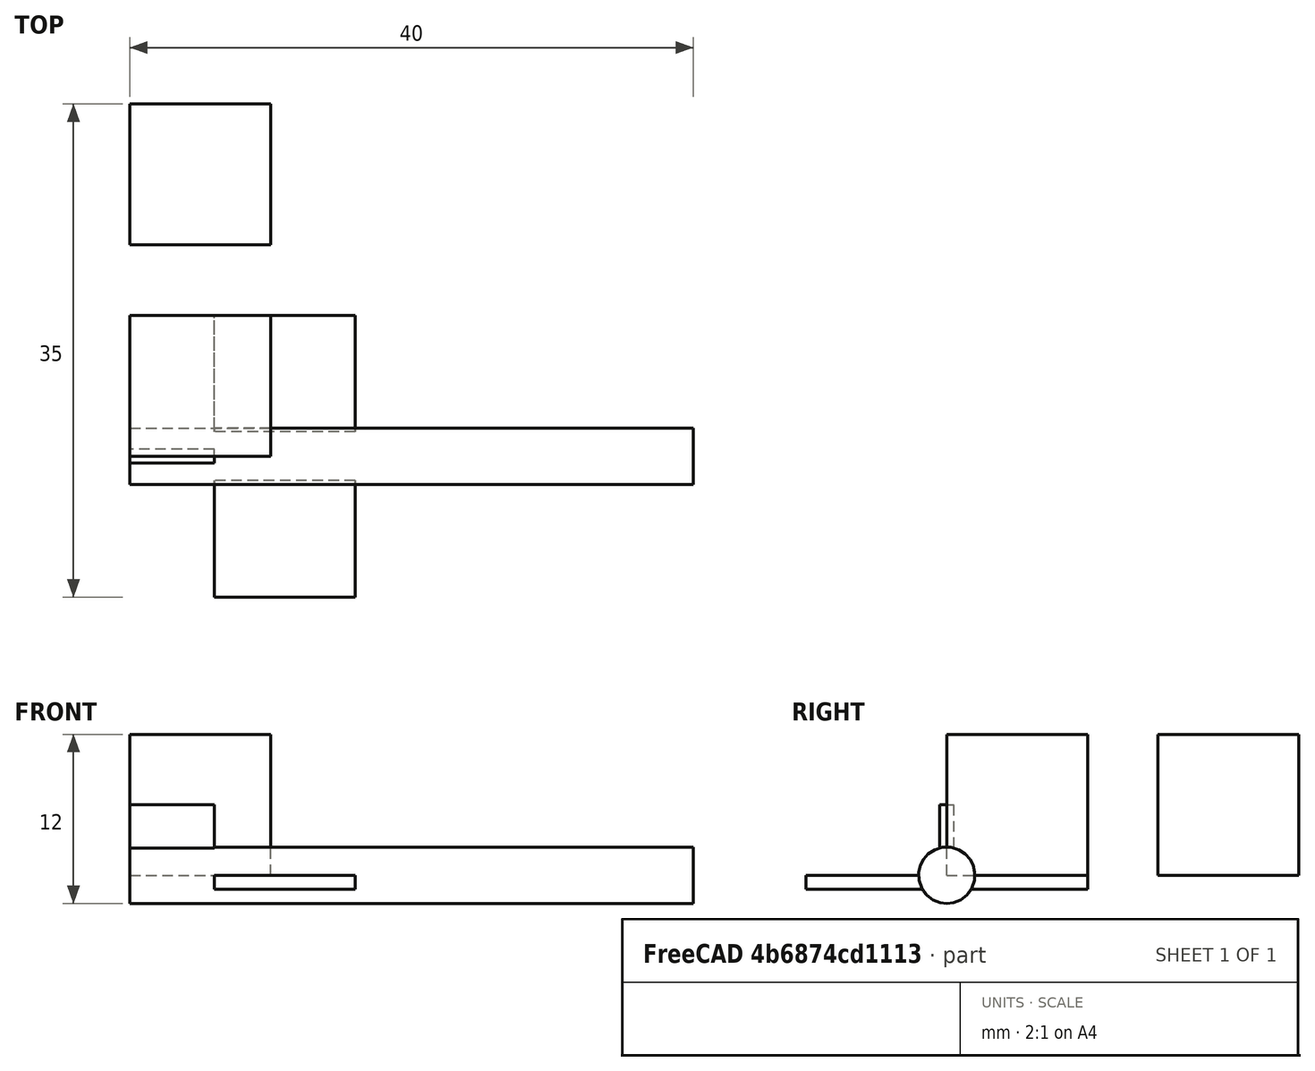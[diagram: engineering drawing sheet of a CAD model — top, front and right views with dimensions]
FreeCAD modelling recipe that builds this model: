
FCSTD DOCUMENT  (FreeCAD 0.21R33694 (Git))
Label: aeroplane_model
License: All rights reserved
LicenseURL: http://en.wikipedia.org/wiki/All_rights_reserved
objects: Part::Box×4, Part::FeaturePython×3, Sketcher::SketchObject×2, Part::Cylinder×1, Part::Fuse×1, Part::MultiFuse×1, Part::Part2DObjectPython×1, Mesh::Feature×1
note: 13 computed .brp shape members not serialized (recipe doc carries the construction recipe); baked Part::Feature solids carry a one-line shape summary decoded from their .brp

FEATURE [Part::Cylinder] Cylinder
  Angle = 360
  AttacherType = Attacher::AttachEngine3D
  FirstAngle = 0
  Height = 20
  Placement = pos=(0,0,0) rot=(0,1,0;1.5708rad)
  Radius = 2
  SecondAngle = 0
FEATURE [Part::Box] Box  label="Cube"
  AttacherType = Attacher::AttachEngine3D
  Height = 1
  Length = 5
  Placement = pos=(3,-10,-1) rot=(0,0,1;0rad)
  Width = 20
FEATURE [Part::Fuse] Fusion
  Base = -> Box
  Tool = -> Cylinder
FEATURE [Part::Box] Box001  label="Cube001"
  AttacherType = Attacher::AttachEngine3D
  Height = 5
  Length = 3
  Placement = pos=(0,-0.5,0) rot=(0,0,1;0rad)
  Width = 1
FEATURE [Part::MultiFuse] Fusion001  label="Aeroplane"
  Shapes = -> [Fusion,Box001]
FEATURE [Part::FeaturePython] Clone  label="Aeroplane001"  # Draft clone (typed FeaturePython)
  AttacherType = Attacher::AttachEngine3D
  Fuse = false
  Objects = -> [Fusion001]
  Scale = (2,1,1)
FEATURE [Part::FeaturePython] PointLight  # WARN: FeaturePython — macro-defined, semantics opaque (R4)
  FadeDistance = 0
  FadePower = 0
  Placement = pos=(10,10,10) rot=(0,0,1;0rad)
FEATURE [Part::Part2DObjectPython] ShapeString  # Draft 2D object (typed FeaturePython)
  FontFile = /Library/Fonts/Arial Unicode.ttf
  MakeFace = true
  Placement = pos=(40.38,1.427e-05,5.29) rot=(0,0.707108,0.707106;3.14159rad)
  Size = 3
  String = Airplane
  Tracking = 0
FEATURE [Sketcher::SketchObject] Sketch
  FullyConstrained = false
  Placement = pos=(1.97e-13,-2.6053e-06,6.808e-12) rot=(1,0,0;0.017453rad)
  sketch-geometry (130):
    g0: LineSegment StartX=38.1366 StartY=-5.29 StartZ=0 EndX=38.4957 EndY=-5.29 EndZ=0
    g1: LineSegment StartX=39.1172 StartY=-7.69699 StartZ=0 EndX=38.1366 EndY=-5.29 EndZ=0
    g2: LineSegment StartX=39.46 StartY=-7.69699 StartZ=0 EndX=39.1172 EndY=-7.69699 EndZ=0
    g3: LineSegment StartX=40.3833 StartY=-5.29 StartZ=0 EndX=39.46 EndY=-7.69699 EndZ=0
    g4: LineSegment StartX=40.0471 StartY=-5.29 StartZ=0 EndX=40.3833 EndY=-5.29 EndZ=0
    g5: LineSegment StartX=39.7814 StartY=-6.02469 StartZ=0 EndX=40.0471 EndY=-5.29 EndZ=0
    g6: LineSegment StartX=38.7778 StartY=-6.02469 StartZ=0 EndX=39.7814 EndY=-6.02469 EndZ=0
    g7: LineSegment StartX=38.4957 StartY=-5.29 StartZ=0 EndX=38.7778 EndY=-6.02469 EndZ=0
    g8: BSplineCurve PolesCount=3 KnotsCount=2 Degree=2 IsPeriodic=0
    g9: LineSegment StartX=39.6912 StartY=-6.27659 StartZ=0 EndX=38.8745 EndY=-6.27659 EndZ=0
    g10: LineSegment StartX=39.4223 StartY=-6.99422 StartZ=0 EndX=39.6912 EndY=-6.27659 EndZ=0
    g11: BSplineCurve PolesCount=3 KnotsCount=2 Degree=2 IsPeriodic=0
    g12: LineSegment StartX=39.2911 StartY=-7.44357 StartZ=0 EndX=39.2993 EndY=-7.44357 EndZ=0
    g13: BSplineCurve PolesCount=3 KnotsCount=2 Degree=2 IsPeriodic=0
    g14: LineSegment StartX=37.6211 StartY=-5.29 StartZ=0 EndX=37.9163 EndY=-5.29 EndZ=0
    g15: LineSegment StartX=37.6211 StartY=-7.03227 StartZ=0 EndX=37.6211 EndY=-5.29 EndZ=0
    g16: LineSegment StartX=37.9163 StartY=-7.03227 StartZ=0 EndX=37.6211 EndY=-7.03227 EndZ=0
    g17: LineSegment StartX=37.9163 StartY=-5.29 StartZ=0 EndX=37.9163 EndY=-7.03227 EndZ=0
    g18: LineSegment StartX=37.6211 StartY=-7.36113 StartZ=0 EndX=37.9163 EndY=-7.36113 EndZ=0
    g19: LineSegment StartX=37.6211 StartY=-7.69699 StartZ=0 EndX=37.6211 EndY=-7.36113 EndZ=0
    g20: LineSegment StartX=37.9163 StartY=-7.69699 StartZ=0 EndX=37.6211 EndY=-7.69699 EndZ=0
    g21: LineSegment StartX=37.9163 StartY=-7.36113 StartZ=0 EndX=37.9163 EndY=-7.69699 EndZ=0
    g22: LineSegment StartX=36.2295 StartY=-6.98121 StartZ=0 EndX=36.3312 EndY=-6.71041 EndZ=0
    g23: BSplineCurve PolesCount=3 KnotsCount=2 Degree=2 IsPeriodic=0
    g24: BSplineCurve PolesCount=3 KnotsCount=2 Degree=2 IsPeriodic=0
    g25: LineSegment StartX=36.9085 StartY=-6.77163 StartZ=0 EndX=36.9019 EndY=-6.77163 EndZ=0
    g26: LineSegment StartX=36.9085 StartY=-7.03227 StartZ=0 EndX=36.9085 EndY=-6.77163 EndZ=0
    g27: LineSegment StartX=37.1774 StartY=-7.03227 StartZ=0 EndX=36.9085 EndY=-7.03227 EndZ=0
    g28: LineSegment StartX=37.1774 StartY=-5.29 StartZ=0 EndX=37.1774 EndY=-7.03227 EndZ=0
    g29: LineSegment StartX=36.8822 StartY=-5.29 StartZ=0 EndX=37.1774 EndY=-5.29 EndZ=0
    g30: LineSegment StartX=36.8822 StartY=-6.20705 StartZ=0 EndX=36.8822 EndY=-5.29 EndZ=0
    g31: BSplineCurve PolesCount=3 KnotsCount=2 Degree=2 IsPeriodic=0
    g32: BSplineCurve PolesCount=3 KnotsCount=2 Degree=2 IsPeriodic=0
    g33: BSplineCurve PolesCount=3 KnotsCount=2 Degree=2 IsPeriodic=0
    g34: BSplineCurve PolesCount=3 KnotsCount=2 Degree=2 IsPeriodic=0
    g35: LineSegment StartX=35.7758 StartY=-6.81055 StartZ=0 EndX=35.7692 EndY=-6.81055 EndZ=0
    g36: LineSegment StartX=35.7758 StartY=-7.03227 StartZ=0 EndX=35.7758 EndY=-6.81055 EndZ=0
    g37: LineSegment StartX=36.0448 StartY=-7.03227 StartZ=0 EndX=35.7758 EndY=-7.03227 EndZ=0
    g38: LineSegment StartX=36.0448 StartY=-4.61828 StartZ=0 EndX=36.0448 EndY=-7.03227 EndZ=0
    g39: LineSegment StartX=35.7496 StartY=-4.61828 StartZ=0 EndX=36.0448 EndY=-4.61828 EndZ=0
    g40: LineSegment StartX=35.7496 StartY=-5.46667 StartZ=0 EndX=35.7496 EndY=-4.61828 EndZ=0
    g41: LineSegment StartX=35.7414 StartY=-5.46667 StartZ=0 EndX=35.7496 EndY=-5.46667 EndZ=0
    g42: BSplineCurve PolesCount=3 KnotsCount=2 Degree=2 IsPeriodic=0
    g43: BSplineCurve PolesCount=3 KnotsCount=2 Degree=2 IsPeriodic=0
    g44: BSplineCurve PolesCount=3 KnotsCount=2 Degree=2 IsPeriodic=0
    g45: BSplineCurve PolesCount=3 KnotsCount=2 Degree=2 IsPeriodic=0
    g46: BSplineCurve PolesCount=3 KnotsCount=2 Degree=2 IsPeriodic=0
    g47: BSplineCurve PolesCount=3 KnotsCount=2 Degree=2 IsPeriodic=0
    g48: BSplineCurve PolesCount=3 KnotsCount=2 Degree=2 IsPeriodic=0
    g49: BSplineCurve PolesCount=3 KnotsCount=2 Degree=2 IsPeriodic=0
    g50: BSplineCurve PolesCount=3 KnotsCount=2 Degree=2 IsPeriodic=0
    g51: BSplineCurve PolesCount=3 KnotsCount=2 Degree=2 IsPeriodic=0
    g52: BSplineCurve PolesCount=3 KnotsCount=2 Degree=2 IsPeriodic=0
    g53: BSplineCurve PolesCount=3 KnotsCount=2 Degree=2 IsPeriodic=0
    g54: BSplineCurve PolesCount=3 KnotsCount=2 Degree=2 IsPeriodic=0
    g55: LineSegment StartX=33.8846 StartY=-5.29 StartZ=0 EndX=34.1798 EndY=-5.29 EndZ=0
    g56: LineSegment StartX=33.8846 StartY=-7.69699 StartZ=0 EndX=33.8846 EndY=-5.29 EndZ=0
    g57: LineSegment StartX=34.1798 StartY=-7.69699 StartZ=0 EndX=33.8846 EndY=-7.69699 EndZ=0
    g58: LineSegment StartX=34.1798 StartY=-5.29 StartZ=0 EndX=34.1798 EndY=-7.69699 EndZ=0
    g59: LineSegment StartX=31.9224 StartY=-5.29 StartZ=0 EndX=32.2323 EndY=-5.29 EndZ=0
    g60: BSplineCurve PolesCount=3 KnotsCount=2 Degree=2 IsPeriodic=0
    g61: BSplineCurve PolesCount=3 KnotsCount=2 Degree=2 IsPeriodic=0
    g62: LineSegment StartX=32.0175 StartY=-6.41806 StartZ=0 EndX=32.0175 EndY=-6.0201 EndZ=0
    g63: BSplineCurve PolesCount=3 KnotsCount=2 Degree=2 IsPeriodic=0
    g64: BSplineCurve PolesCount=3 KnotsCount=2 Degree=2 IsPeriodic=0
    g65: BSplineCurve PolesCount=3 KnotsCount=2 Degree=2 IsPeriodic=0
    g66: BSplineCurve PolesCount=3 KnotsCount=2 Degree=2 IsPeriodic=0
    g67: BSplineCurve PolesCount=3 KnotsCount=2 Degree=2 IsPeriodic=0
    g68: LineSegment StartX=33.1884 StartY=-6.50049 StartZ=0 EndX=33.477 EndY=-6.53821 EndZ=0
    g69: BSplineCurve PolesCount=3 KnotsCount=2 Degree=2 IsPeriodic=0
    g70: BSplineCurve PolesCount=3 KnotsCount=2 Degree=2 IsPeriodic=0
    g71: BSplineCurve PolesCount=3 KnotsCount=2 Degree=2 IsPeriodic=0
    g72: BSplineCurve PolesCount=3 KnotsCount=2 Degree=2 IsPeriodic=0
    g73: BSplineCurve PolesCount=3 KnotsCount=2 Degree=2 IsPeriodic=0
    g74: BSplineCurve PolesCount=3 KnotsCount=2 Degree=2 IsPeriodic=0
    g75: BSplineCurve PolesCount=3 KnotsCount=2 Degree=2 IsPeriodic=0
    g76: LineSegment StartX=32.8424 StartY=-6.29375 StartZ=0 EndX=32.5669 EndY=-6.33475 EndZ=0
    g77: BSplineCurve PolesCount=3 KnotsCount=2 Degree=2 IsPeriodic=0
    g78: BSplineCurve PolesCount=3 KnotsCount=2 Degree=2 IsPeriodic=0
    g79: BSplineCurve PolesCount=3 KnotsCount=2 Degree=2 IsPeriodic=0
    g80: BSplineCurve PolesCount=3 KnotsCount=2 Degree=2 IsPeriodic=0
    g81: BSplineCurve PolesCount=3 KnotsCount=2 Degree=2 IsPeriodic=0
    g82: BSplineCurve PolesCount=3 KnotsCount=2 Degree=2 IsPeriodic=0
    g83: LineSegment StartX=32.3127 StartY=-6.05246 StartZ=0 EndX=32.3127 EndY=-6.15764 EndZ=0
    g84: BSplineCurve PolesCount=3 KnotsCount=2 Degree=2 IsPeriodic=0
    g85: BSplineCurve PolesCount=3 KnotsCount=2 Degree=2 IsPeriodic=0
    g86: BSplineCurve PolesCount=3 KnotsCount=2 Degree=2 IsPeriodic=0
    g87: BSplineCurve PolesCount=3 KnotsCount=2 Degree=2 IsPeriodic=0
    g88: BSplineCurve PolesCount=3 KnotsCount=2 Degree=2 IsPeriodic=0
    g89: BSplineCurve PolesCount=3 KnotsCount=2 Degree=2 IsPeriodic=0
    g90: LineSegment StartX=30.1411 StartY=-5.29 StartZ=0 EndX=30.4379 EndY=-5.29 EndZ=0
    g91: LineSegment StartX=30.1411 StartY=-6.36383 StartZ=0 EndX=30.1411 EndY=-5.29 EndZ=0
    g92: BSplineCurve PolesCount=3 KnotsCount=2 Degree=2 IsPeriodic=0
    g93: BSplineCurve PolesCount=3 KnotsCount=2 Degree=2 IsPeriodic=0
    g94: BSplineCurve PolesCount=3 KnotsCount=2 Degree=2 IsPeriodic=0
    g95: BSplineCurve PolesCount=3 KnotsCount=2 Degree=2 IsPeriodic=0
    g96: BSplineCurve PolesCount=3 KnotsCount=2 Degree=2 IsPeriodic=0
    g97: BSplineCurve PolesCount=3 KnotsCount=2 Degree=2 IsPeriodic=0
    g98: LineSegment StartX=31.294 StartY=-6.78814 StartZ=0 EndX=31.2874 EndY=-6.78814 EndZ=0
    g99: LineSegment StartX=31.294 StartY=-7.03227 StartZ=0 EndX=31.294 EndY=-6.78814 EndZ=0
    g100: LineSegment StartX=31.5596 StartY=-7.03227 StartZ=0 EndX=31.294 EndY=-7.03227 EndZ=0
    g101: LineSegment StartX=31.5596 StartY=-5.29 StartZ=0 EndX=31.5596 EndY=-7.03227 EndZ=0
    g102: LineSegment StartX=31.2644 StartY=-5.29 StartZ=0 EndX=31.5596 EndY=-5.29 EndZ=0
    g103: LineSegment StartX=31.2644 StartY=-6.24565 StartZ=0 EndX=31.2644 EndY=-5.29 EndZ=0
    g104: BSplineCurve PolesCount=3 KnotsCount=2 Degree=2 IsPeriodic=0
    g105: BSplineCurve PolesCount=3 KnotsCount=2 Degree=2 IsPeriodic=0
    g106: BSplineCurve PolesCount=3 KnotsCount=2 Degree=2 IsPeriodic=0
    g107: BSplineCurve PolesCount=3 KnotsCount=2 Degree=2 IsPeriodic=0
    g108: BSplineCurve PolesCount=3 KnotsCount=2 Degree=2 IsPeriodic=0
    g109: LineSegment StartX=30.4379 StartY=-5.29 StartZ=0 EndX=30.4379 EndY=-6.35279 EndZ=0
    g110: LineSegment StartX=28.1827 StartY=-6.08767 StartZ=0 EndX=29.4864 EndY=-6.08767 EndZ=0
    g111: BSplineCurve PolesCount=3 KnotsCount=2 Degree=2 IsPeriodic=0
    g112: BSplineCurve PolesCount=3 KnotsCount=2 Degree=2 IsPeriodic=0
    g113: BSplineCurve PolesCount=3 KnotsCount=2 Degree=2 IsPeriodic=0
    g114: BSplineCurve PolesCount=3 KnotsCount=2 Degree=2 IsPeriodic=0
    g115: BSplineCurve PolesCount=3 KnotsCount=2 Degree=2 IsPeriodic=0
    g116: BSplineCurve PolesCount=3 KnotsCount=2 Degree=2 IsPeriodic=0
    g117: BSplineCurve PolesCount=3 KnotsCount=2 Degree=2 IsPeriodic=0
    g118: BSplineCurve PolesCount=3 KnotsCount=2 Degree=2 IsPeriodic=0
    g119: BSplineCurve PolesCount=3 KnotsCount=2 Degree=2 IsPeriodic=0
    g120: LineSegment StartX=28.4959 StartY=-5.84976 StartZ=0 EndX=28.1925 EndY=-5.81205 EndZ=0
    g121: BSplineCurve PolesCount=3 KnotsCount=2 Degree=2 IsPeriodic=0
    g122: BSplineCurve PolesCount=3 KnotsCount=2 Degree=2 IsPeriodic=0
    g123: BSplineCurve PolesCount=3 KnotsCount=2 Degree=2 IsPeriodic=0
    g124: BSplineCurve PolesCount=3 KnotsCount=2 Degree=2 IsPeriodic=0
    g125: BSplineCurve PolesCount=3 KnotsCount=2 Degree=2 IsPeriodic=0
    g126: LineSegment StartX=29.47 StartY=-6.32557 StartZ=0 EndX=28.4861 EndY=-6.32557 EndZ=0
    g127: BSplineCurve PolesCount=3 KnotsCount=2 Degree=2 IsPeriodic=0
    g128: BSplineCurve PolesCount=3 KnotsCount=2 Degree=2 IsPeriodic=0
    g129: BSplineCurve PolesCount=3 KnotsCount=2 Degree=2 IsPeriodic=0
  constraints (172):
    c: Horizontal(g0)
    c: Coincident(g0,g1)
    c: Coincident(g1,g2)
    c: Horizontal(g2)
    c: Coincident(g2,g3)
    c: Coincident(g3,g4)
    c: Horizontal(g4)
    c: Coincident(g4,g5)
    c: Coincident(g5,g6)
    c: Horizontal(g6)
    c: Coincident(g6,g7)
    c: Coincident(g7,g0)
    c: Coincident(g8,g9)
    c: Horizontal(g9)
    c: Coincident(g9,g10)
    c: Coincident(g10,g11)
    c: Coincident(g11,g12)
    c: Horizontal(g12)
    c: Coincident(g12,g13)
    c: Coincident(g13,g8)
    c: Horizontal(g14)
    c: Coincident(g14,g15)
    c: Vertical(g15)
    c: Coincident(g15,g16)
    c: Horizontal(g16)
    c: Coincident(g16,g17)
    c: Vertical(g17)
    c: Coincident(g17,g14)
    c: Horizontal(g18)
    c: Coincident(g18,g19)
    c: Vertical(g19)
    c: Coincident(g19,g20)
    c: Horizontal(g20)
    c: Coincident(g20,g21)
    c: Coincident(g21,g18)
    c: Coincident(g22,g23)
    c: Coincident(g23,g24)
    c: Coincident(g24,g25)
    c: Horizontal(g25)
    c: Coincident(g25,g26)
    c: Vertical(g26)
    c: Coincident(g26,g27)
    c: Horizontal(g27)
    c: Coincident(g27,g28)
    c: Vertical(g28)
    c: Coincident(g28,g29)
    c: Horizontal(g29)
    c: Coincident(g29,g30)
    c: Coincident(g30,g31)
    c: Coincident(g31,g32)
    c: Coincident(g32,g33)
    c: Coincident(g33,g22)
    c: Coincident(g34,g35)
    c: Horizontal(g35)
    c: Coincident(g35,g36)
    c: Vertical(g36)
    c: Coincident(g36,g37)
    c: Horizontal(g37)
    c: Coincident(g37,g38)
    c: Vertical(g38)
    c: Coincident(g38,g39)
    c: Horizontal(g39)
    c: Coincident(g39,g40)
    c: Vertical(g40)
    c: Coincident(g40,g41)
    c: Horizontal(g41)
    c: Coincident(g41,g42)
    c: Coincident(g42,g43)
    c: Coincident(g43,g44)
    c: Coincident(g44,g45)
    c: Coincident(g45,g46)
    c: Coincident(g46,g34)
    c: Coincident(g47,g48)
    c: Coincident(g48,g49)
    c: Coincident(g49,g50)
    c: Coincident(g50,g51)
    c: Coincident(g51,g52)
    c: Coincident(g52,g53)
    c: Coincident(g53,g54)
    c: Coincident(g54,g47)
    c: Horizontal(g55)
    c: Coincident(g55,g56)
    c: Vertical(g56)
    c: Coincident(g56,g57)
    c: Horizontal(g57)
    c: Coincident(g57,g58)
    c: Vertical(g58)
    c: Coincident(g58,g55)
    c: Horizontal(g59)
    c: Coincident(g59,g60)
    c: Coincident(g60,g61)
    c: Coincident(g61,g62)
    c: Vertical(g62)
    c: Coincident(g62,g63)
    c: Coincident(g63,g64)
    c: Coincident(g64,g65)
    c: Coincident(g65,g66)
    c: Coincident(g66,g67)
    c: Coincident(g67,g68)
    c: Coincident(g68,g69)
    c: Coincident(g69,g70)
    c: Coincident(g70,g71)
    c: Coincident(g71,g72)
    c: Coincident(g72,g73)
    c: Coincident(g73,g74)
    c: Coincident(g74,g75)
    c: Coincident(g75,g76)
    c: Coincident(g76,g77)
    c: Coincident(g77,g78)
    c: Coincident(g78,g79)
    c: Coincident(g79,g80)
    c: Coincident(g80,g81)
    c: Coincident(g81,g82)
    c: Coincident(g82,g59)
    c: Vertical(g83)
    c: Coincident(g83,g84)
    c: Coincident(g84,g85)
    c: Coincident(g85,g86)
    c: Coincident(g86,g87)
    c: Coincident(g87,g88)
    c: Coincident(g88,g89)
    c: Coincident(g89,g83)
    c: Horizontal(g90)
    c: Coincident(g90,g91)
    c: Vertical(g91)
    c: Coincident(g91,g92)
    c: Coincident(g92,g93)
    c: Coincident(g93,g94)
    c: Coincident(g94,g95)
    c: Coincident(g95,g96)
    c: Coincident(g96,g97)
    c: Coincident(g97,g98)
    c: Horizontal(g98)
    c: Coincident(g98,g99)
    c: Vertical(g99)
    c: Coincident(g99,g100)
    c: Horizontal(g100)
    c: Coincident(g100,g101)
    c: Vertical(g101)
    c: Coincident(g101,g102)
    c: Horizontal(g102)
    c: Coincident(g102,g103)
    c: Vertical(g103)
    c: Coincident(g103,g104)
    c: Coincident(g104,g105)
    c: Coincident(g105,g106)
    c: Coincident(g106,g107)
    c: Coincident(g107,g108)
    c: Coincident(g108,g109)
    c: Vertical(g109)
    c: Coincident(g109,g90)
    c: Coincident(g110,g111)
    c: Coincident(g111,g112)
    c: Coincident(g112,g113)
    c: Coincident(g113,g114)
    c: Coincident(g114,g115)
    c: Coincident(g115,g116)
    c: Coincident(g116,g117)
    c: Coincident(g117,g118)
    c: Coincident(g118,g119)
    c: Coincident(g119,g120)
    c: Coincident(g120,g121)
    c: Coincident(g121,g122)
    c: Coincident(g122,g123)
    c: Coincident(g123,g124)
    c: Coincident(g124,g110)
    c: Coincident(g125,g126)
    c: Horizontal(g126)
    c: Coincident(g126,g127)
    c: Coincident(g127,g128)
    c: Coincident(g128,g129)
    c: Coincident(g129,g125)
FEATURE [Sketcher::SketchObject] Mapped_Sketch
  FullyConstrained = false
  Support = -> [Fusion001]
  sketch-geometry (134):
    g0: LineSegment StartX=27.4831 StartY=-8.86191 StartZ=0 EndX=41.7478 EndY=-8.86191 EndZ=0
    g1: LineSegment StartX=41.6977 StartY=-8.96223 StartZ=0 EndX=41.6977 EndY=-3.46947 EndZ=0
    g2: LineSegment StartX=41.6614 StartY=-3.47708 StartZ=0 EndX=27.4525 EndY=-3.47708 EndZ=0
    g3: LineSegment StartX=27.4831 StartY=-3.47708 StartZ=0 EndX=27.4831 EndY=-8.86191 EndZ=0
    g4: LineSegment StartX=38.1366 StartY=-5.29 StartZ=0 EndX=38.4957 EndY=-5.29 EndZ=0
    g5: LineSegment StartX=39.1172 StartY=-7.69699 StartZ=0 EndX=38.1366 EndY=-5.29 EndZ=0
    g6: LineSegment StartX=39.46 StartY=-7.69699 StartZ=0 EndX=39.1172 EndY=-7.69699 EndZ=0
    g7: LineSegment StartX=40.3833 StartY=-5.29 StartZ=0 EndX=39.46 EndY=-7.69699 EndZ=0
    g8: LineSegment StartX=40.0471 StartY=-5.29 StartZ=0 EndX=40.3833 EndY=-5.29 EndZ=0
    g9: LineSegment StartX=39.7814 StartY=-6.02469 StartZ=0 EndX=40.0471 EndY=-5.29 EndZ=0
    g10: LineSegment StartX=38.7778 StartY=-6.02469 StartZ=0 EndX=39.7814 EndY=-6.02469 EndZ=0
    g11: LineSegment StartX=38.4957 StartY=-5.29 StartZ=0 EndX=38.7778 EndY=-6.02469 EndZ=0
    g12: BSplineCurve PolesCount=3 KnotsCount=2 Degree=2 IsPeriodic=0
    g13: LineSegment StartX=39.6912 StartY=-6.27659 StartZ=0 EndX=38.8745 EndY=-6.27659 EndZ=0
    g14: LineSegment StartX=39.4223 StartY=-6.99422 StartZ=0 EndX=39.6912 EndY=-6.27659 EndZ=0
    g15: BSplineCurve PolesCount=3 KnotsCount=2 Degree=2 IsPeriodic=0
    g16: LineSegment StartX=39.2911 StartY=-7.44357 StartZ=0 EndX=39.2993 EndY=-7.44357 EndZ=0
    g17: BSplineCurve PolesCount=3 KnotsCount=2 Degree=2 IsPeriodic=0
    g18: LineSegment StartX=37.6211 StartY=-5.29 StartZ=0 EndX=37.9163 EndY=-5.29 EndZ=0
    g19: LineSegment StartX=37.6211 StartY=-7.03227 StartZ=0 EndX=37.6211 EndY=-5.29 EndZ=0
    g20: LineSegment StartX=37.9163 StartY=-7.03227 StartZ=0 EndX=37.6211 EndY=-7.03227 EndZ=0
    g21: LineSegment StartX=37.9163 StartY=-5.29 StartZ=0 EndX=37.9163 EndY=-7.03227 EndZ=0
    g22: LineSegment StartX=37.6211 StartY=-7.36113 StartZ=0 EndX=37.9163 EndY=-7.36113 EndZ=0
    g23: LineSegment StartX=37.6211 StartY=-7.69699 StartZ=0 EndX=37.6211 EndY=-7.36113 EndZ=0
    g24: LineSegment StartX=37.9163 StartY=-7.69699 StartZ=0 EndX=37.6211 EndY=-7.69699 EndZ=0
    g25: LineSegment StartX=37.9163 StartY=-7.36113 StartZ=0 EndX=37.9163 EndY=-7.69699 EndZ=0
    g26: LineSegment StartX=36.2295 StartY=-6.98121 StartZ=0 EndX=36.3312 EndY=-6.71041 EndZ=0
    g27: BSplineCurve PolesCount=3 KnotsCount=2 Degree=2 IsPeriodic=0
    g28: BSplineCurve PolesCount=3 KnotsCount=2 Degree=2 IsPeriodic=0
    g29: LineSegment StartX=36.9085 StartY=-6.77163 StartZ=0 EndX=36.9019 EndY=-6.77163 EndZ=0
    g30: LineSegment StartX=36.9085 StartY=-7.03227 StartZ=0 EndX=36.9085 EndY=-6.77163 EndZ=0
    g31: LineSegment StartX=37.1774 StartY=-7.03227 StartZ=0 EndX=36.9085 EndY=-7.03227 EndZ=0
    g32: LineSegment StartX=37.1774 StartY=-5.29 StartZ=0 EndX=37.1774 EndY=-7.03227 EndZ=0
    g33: LineSegment StartX=36.8822 StartY=-5.29 StartZ=0 EndX=37.1774 EndY=-5.29 EndZ=0
    g34: LineSegment StartX=36.8822 StartY=-6.20705 StartZ=0 EndX=36.8822 EndY=-5.29 EndZ=0
    g35: BSplineCurve PolesCount=3 KnotsCount=2 Degree=2 IsPeriodic=0
    g36: BSplineCurve PolesCount=3 KnotsCount=2 Degree=2 IsPeriodic=0
    g37: BSplineCurve PolesCount=3 KnotsCount=2 Degree=2 IsPeriodic=0
    g38: BSplineCurve PolesCount=3 KnotsCount=2 Degree=2 IsPeriodic=0
    g39: LineSegment StartX=35.7758 StartY=-6.81055 StartZ=0 EndX=35.7692 EndY=-6.81055 EndZ=0
    g40: LineSegment StartX=35.7758 StartY=-7.03227 StartZ=0 EndX=35.7758 EndY=-6.81055 EndZ=0
    g41: LineSegment StartX=36.0448 StartY=-7.03227 StartZ=0 EndX=35.7758 EndY=-7.03227 EndZ=0
    g42: LineSegment StartX=36.0448 StartY=-4.61828 StartZ=0 EndX=36.0448 EndY=-7.03227 EndZ=0
    g43: LineSegment StartX=35.7496 StartY=-4.61828 StartZ=0 EndX=36.0448 EndY=-4.61828 EndZ=0
    g44: LineSegment StartX=35.7496 StartY=-5.46667 StartZ=0 EndX=35.7496 EndY=-4.61828 EndZ=0
    g45: LineSegment StartX=35.7414 StartY=-5.46667 StartZ=0 EndX=35.7496 EndY=-5.46667 EndZ=0
    g46: BSplineCurve PolesCount=3 KnotsCount=2 Degree=2 IsPeriodic=0
    g47: BSplineCurve PolesCount=3 KnotsCount=2 Degree=2 IsPeriodic=0
    g48: BSplineCurve PolesCount=3 KnotsCount=2 Degree=2 IsPeriodic=0
    g49: BSplineCurve PolesCount=3 KnotsCount=2 Degree=2 IsPeriodic=0
    g50: BSplineCurve PolesCount=3 KnotsCount=2 Degree=2 IsPeriodic=0
    g51: BSplineCurve PolesCount=3 KnotsCount=2 Degree=2 IsPeriodic=0
    g52: BSplineCurve PolesCount=3 KnotsCount=2 Degree=2 IsPeriodic=0
    g53: BSplineCurve PolesCount=3 KnotsCount=2 Degree=2 IsPeriodic=0
    g54: BSplineCurve PolesCount=3 KnotsCount=2 Degree=2 IsPeriodic=0
    g55: BSplineCurve PolesCount=3 KnotsCount=2 Degree=2 IsPeriodic=0
    g56: BSplineCurve PolesCount=3 KnotsCount=2 Degree=2 IsPeriodic=0
    g57: BSplineCurve PolesCount=3 KnotsCount=2 Degree=2 IsPeriodic=0
    g58: BSplineCurve PolesCount=3 KnotsCount=2 Degree=2 IsPeriodic=0
    g59: LineSegment StartX=33.8846 StartY=-5.29 StartZ=0 EndX=34.1798 EndY=-5.29 EndZ=0
    g60: LineSegment StartX=33.8846 StartY=-7.69699 StartZ=0 EndX=33.8846 EndY=-5.29 EndZ=0
    g61: LineSegment StartX=34.1798 StartY=-7.69699 StartZ=0 EndX=33.8846 EndY=-7.69699 EndZ=0
    g62: LineSegment StartX=34.1798 StartY=-5.29 StartZ=0 EndX=34.1798 EndY=-7.69699 EndZ=0
    g63: LineSegment StartX=31.9224 StartY=-5.29 StartZ=0 EndX=32.2323 EndY=-5.29 EndZ=0
    g64: BSplineCurve PolesCount=3 KnotsCount=2 Degree=2 IsPeriodic=0
    g65: BSplineCurve PolesCount=3 KnotsCount=2 Degree=2 IsPeriodic=0
    g66: LineSegment StartX=32.0175 StartY=-6.41806 StartZ=0 EndX=32.0175 EndY=-6.0201 EndZ=0
    g67: BSplineCurve PolesCount=3 KnotsCount=2 Degree=2 IsPeriodic=0
    g68: BSplineCurve PolesCount=3 KnotsCount=2 Degree=2 IsPeriodic=0
    g69: BSplineCurve PolesCount=3 KnotsCount=2 Degree=2 IsPeriodic=0
    g70: BSplineCurve PolesCount=3 KnotsCount=2 Degree=2 IsPeriodic=0
    g71: BSplineCurve PolesCount=3 KnotsCount=2 Degree=2 IsPeriodic=0
    g72: LineSegment StartX=33.1884 StartY=-6.50049 StartZ=0 EndX=33.477 EndY=-6.53821 EndZ=0
    g73: BSplineCurve PolesCount=3 KnotsCount=2 Degree=2 IsPeriodic=0
    g74: BSplineCurve PolesCount=3 KnotsCount=2 Degree=2 IsPeriodic=0
    g75: BSplineCurve PolesCount=3 KnotsCount=2 Degree=2 IsPeriodic=0
    g76: BSplineCurve PolesCount=3 KnotsCount=2 Degree=2 IsPeriodic=0
    g77: BSplineCurve PolesCount=3 KnotsCount=2 Degree=2 IsPeriodic=0
    g78: BSplineCurve PolesCount=3 KnotsCount=2 Degree=2 IsPeriodic=0
    g79: BSplineCurve PolesCount=3 KnotsCount=2 Degree=2 IsPeriodic=0
    g80: LineSegment StartX=32.8424 StartY=-6.29375 StartZ=0 EndX=32.5669 EndY=-6.33475 EndZ=0
    g81: BSplineCurve PolesCount=3 KnotsCount=2 Degree=2 IsPeriodic=0
    g82: BSplineCurve PolesCount=3 KnotsCount=2 Degree=2 IsPeriodic=0
    g83: BSplineCurve PolesCount=3 KnotsCount=2 Degree=2 IsPeriodic=0
    g84: BSplineCurve PolesCount=3 KnotsCount=2 Degree=2 IsPeriodic=0
    g85: BSplineCurve PolesCount=3 KnotsCount=2 Degree=2 IsPeriodic=0
    g86: BSplineCurve PolesCount=3 KnotsCount=2 Degree=2 IsPeriodic=0
    g87: LineSegment StartX=32.3127 StartY=-6.05246 StartZ=0 EndX=32.3127 EndY=-6.15764 EndZ=0
    g88: BSplineCurve PolesCount=3 KnotsCount=2 Degree=2 IsPeriodic=0
    g89: BSplineCurve PolesCount=3 KnotsCount=2 Degree=2 IsPeriodic=0
    g90: BSplineCurve PolesCount=3 KnotsCount=2 Degree=2 IsPeriodic=0
    g91: BSplineCurve PolesCount=3 KnotsCount=2 Degree=2 IsPeriodic=0
    g92: BSplineCurve PolesCount=3 KnotsCount=2 Degree=2 IsPeriodic=0
    g93: BSplineCurve PolesCount=3 KnotsCount=2 Degree=2 IsPeriodic=0
    g94: LineSegment StartX=30.1411 StartY=-5.29 StartZ=0 EndX=30.4379 EndY=-5.29 EndZ=0
    g95: LineSegment StartX=30.1411 StartY=-6.36383 StartZ=0 EndX=30.1411 EndY=-5.29 EndZ=0
    g96: BSplineCurve PolesCount=3 KnotsCount=2 Degree=2 IsPeriodic=0
    g97: BSplineCurve PolesCount=3 KnotsCount=2 Degree=2 IsPeriodic=0
    g98: BSplineCurve PolesCount=3 KnotsCount=2 Degree=2 IsPeriodic=0
    g99: BSplineCurve PolesCount=3 KnotsCount=2 Degree=2 IsPeriodic=0
    g100: BSplineCurve PolesCount=3 KnotsCount=2 Degree=2 IsPeriodic=0
    g101: BSplineCurve PolesCount=3 KnotsCount=2 Degree=2 IsPeriodic=0
    g102: LineSegment StartX=31.294 StartY=-6.78814 StartZ=0 EndX=31.2874 EndY=-6.78814 EndZ=0
    g103: LineSegment StartX=31.294 StartY=-7.03227 StartZ=0 EndX=31.294 EndY=-6.78814 EndZ=0
    g104: LineSegment StartX=31.5596 StartY=-7.03227 StartZ=0 EndX=31.294 EndY=-7.03227 EndZ=0
    g105: LineSegment StartX=31.5596 StartY=-5.29 StartZ=0 EndX=31.5596 EndY=-7.03227 EndZ=0
    g106: LineSegment StartX=31.2644 StartY=-5.29 StartZ=0 EndX=31.5596 EndY=-5.29 EndZ=0
    g107: LineSegment StartX=31.2644 StartY=-6.24565 StartZ=0 EndX=31.2644 EndY=-5.29 EndZ=0
    g108: BSplineCurve PolesCount=3 KnotsCount=2 Degree=2 IsPeriodic=0
    g109: BSplineCurve PolesCount=3 KnotsCount=2 Degree=2 IsPeriodic=0
    g110: BSplineCurve PolesCount=3 KnotsCount=2 Degree=2 IsPeriodic=0
    g111: BSplineCurve PolesCount=3 KnotsCount=2 Degree=2 IsPeriodic=0
    g112: BSplineCurve PolesCount=3 KnotsCount=2 Degree=2 IsPeriodic=0
    g113: LineSegment StartX=30.4379 StartY=-5.29 StartZ=0 EndX=30.4379 EndY=-6.35279 EndZ=0
    g114: LineSegment StartX=28.1827 StartY=-6.08767 StartZ=0 EndX=29.4864 EndY=-6.08767 EndZ=0
    g115: BSplineCurve PolesCount=3 KnotsCount=2 Degree=2 IsPeriodic=0
    g116: BSplineCurve PolesCount=3 KnotsCount=2 Degree=2 IsPeriodic=0
    g117: BSplineCurve PolesCount=3 KnotsCount=2 Degree=2 IsPeriodic=0
    g118: BSplineCurve PolesCount=3 KnotsCount=2 Degree=2 IsPeriodic=0
    g119: BSplineCurve PolesCount=3 KnotsCount=2 Degree=2 IsPeriodic=0
    g120: BSplineCurve PolesCount=3 KnotsCount=2 Degree=2 IsPeriodic=0
    g121: BSplineCurve PolesCount=3 KnotsCount=2 Degree=2 IsPeriodic=0
    g122: BSplineCurve PolesCount=3 KnotsCount=2 Degree=2 IsPeriodic=0
    g123: BSplineCurve PolesCount=3 KnotsCount=2 Degree=2 IsPeriodic=0
    g124: LineSegment StartX=28.4959 StartY=-5.84976 StartZ=0 EndX=28.1925 EndY=-5.81205 EndZ=0
    g125: BSplineCurve PolesCount=3 KnotsCount=2 Degree=2 IsPeriodic=0
    g126: BSplineCurve PolesCount=3 KnotsCount=2 Degree=2 IsPeriodic=0
    g127: BSplineCurve PolesCount=3 KnotsCount=2 Degree=2 IsPeriodic=0
    g128: BSplineCurve PolesCount=3 KnotsCount=2 Degree=2 IsPeriodic=0
    g129: BSplineCurve PolesCount=3 KnotsCount=2 Degree=2 IsPeriodic=0
    g130: LineSegment StartX=29.47 StartY=-6.32557 StartZ=0 EndX=28.4861 EndY=-6.32557 EndZ=0
    g131: BSplineCurve PolesCount=3 KnotsCount=2 Degree=2 IsPeriodic=0
    g132: BSplineCurve PolesCount=3 KnotsCount=2 Degree=2 IsPeriodic=0
    g133: BSplineCurve PolesCount=3 KnotsCount=2 Degree=2 IsPeriodic=0
  constraints (176):
    c: Horizontal(g2)
    c: Horizontal(g0)
    c: Vertical(g3)
    c: Vertical(g1)
    c: Horizontal(g4)
    c: Coincident(g4,g5)
    c: Coincident(g5,g6)
    c: Horizontal(g6)
    c: Coincident(g6,g7)
    c: Coincident(g7,g8)
    c: Horizontal(g8)
    c: Coincident(g8,g9)
    c: Coincident(g9,g10)
    c: Horizontal(g10)
    c: Coincident(g10,g11)
    c: Coincident(g11,g4)
    c: Coincident(g12,g13)
    c: Horizontal(g13)
    c: Coincident(g13,g14)
    c: Coincident(g14,g15)
    c: Coincident(g15,g16)
    c: Horizontal(g16)
    c: Coincident(g16,g17)
    c: Coincident(g17,g12)
    c: Horizontal(g18)
    c: Coincident(g18,g19)
    c: Vertical(g19)
    c: Coincident(g19,g20)
    c: Horizontal(g20)
    c: Coincident(g20,g21)
    c: Vertical(g21)
    c: Coincident(g21,g18)
    c: Horizontal(g22)
    c: Coincident(g22,g23)
    c: Vertical(g23)
    c: Coincident(g23,g24)
    c: Horizontal(g24)
    c: Coincident(g24,g25)
    c: Coincident(g25,g22)
    c: Coincident(g26,g27)
    c: Coincident(g27,g28)
    c: Coincident(g28,g29)
    c: Horizontal(g29)
    c: Coincident(g29,g30)
    c: Vertical(g30)
    c: Coincident(g30,g31)
    c: Horizontal(g31)
    c: Coincident(g31,g32)
    c: Vertical(g32)
    c: Coincident(g32,g33)
    c: Horizontal(g33)
    c: Coincident(g33,g34)
    c: Coincident(g34,g35)
    c: Coincident(g35,g36)
    c: Coincident(g36,g37)
    c: Coincident(g37,g26)
    c: Coincident(g38,g39)
    c: Horizontal(g39)
    c: Coincident(g39,g40)
    c: Vertical(g40)
    c: Coincident(g40,g41)
    c: Horizontal(g41)
    c: Coincident(g41,g42)
    c: Vertical(g42)
    c: Coincident(g42,g43)
    c: Horizontal(g43)
    c: Coincident(g43,g44)
    c: Vertical(g44)
    c: Coincident(g44,g45)
    c: Horizontal(g45)
    c: Coincident(g45,g46)
    c: Coincident(g46,g47)
    c: Coincident(g47,g48)
    c: Coincident(g48,g49)
    c: Coincident(g49,g50)
    c: Coincident(g50,g38)
    c: Coincident(g51,g52)
    c: Coincident(g52,g53)
    c: Coincident(g53,g54)
    c: Coincident(g54,g55)
    c: Coincident(g55,g56)
    c: Coincident(g56,g57)
    c: Coincident(g57,g58)
    c: Coincident(g58,g51)
    c: Horizontal(g59)
    c: Coincident(g59,g60)
    c: Vertical(g60)
    c: Coincident(g60,g61)
    c: Horizontal(g61)
    c: Coincident(g61,g62)
    c: Vertical(g62)
    c: Coincident(g62,g59)
    c: Horizontal(g63)
    c: Coincident(g63,g64)
    c: Coincident(g64,g65)
    c: Coincident(g65,g66)
    c: Vertical(g66)
    c: Coincident(g66,g67)
    c: Coincident(g67,g68)
    c: Coincident(g68,g69)
    c: Coincident(g69,g70)
    c: Coincident(g70,g71)
    c: Coincident(g71,g72)
    c: Coincident(g72,g73)
    c: Coincident(g73,g74)
    c: Coincident(g74,g75)
    c: Coincident(g75,g76)
    c: Coincident(g76,g77)
    c: Coincident(g77,g78)
    c: Coincident(g78,g79)
    c: Coincident(g79,g80)
    c: Coincident(g80,g81)
    c: Coincident(g81,g82)
    c: Coincident(g82,g83)
    c: Coincident(g83,g84)
    c: Coincident(g84,g85)
    c: Coincident(g85,g86)
    c: Coincident(g86,g63)
    c: Vertical(g87)
    c: Coincident(g87,g88)
    c: Coincident(g88,g89)
    c: Coincident(g89,g90)
    c: Coincident(g90,g91)
    c: Coincident(g91,g92)
    c: Coincident(g92,g93)
    c: Coincident(g93,g87)
    c: Horizontal(g94)
    c: Coincident(g94,g95)
    c: Vertical(g95)
    c: Coincident(g95,g96)
    c: Coincident(g96,g97)
    c: Coincident(g97,g98)
    c: Coincident(g98,g99)
    c: Coincident(g99,g100)
    c: Coincident(g100,g101)
    c: Coincident(g101,g102)
    c: Horizontal(g102)
    c: Coincident(g102,g103)
    c: Vertical(g103)
    c: Coincident(g103,g104)
    c: Horizontal(g104)
    c: Coincident(g104,g105)
    c: Vertical(g105)
    c: Coincident(g105,g106)
    c: Horizontal(g106)
    c: Coincident(g106,g107)
    c: Vertical(g107)
    c: Coincident(g107,g108)
    c: Coincident(g108,g109)
    c: Coincident(g109,g110)
    c: Coincident(g110,g111)
    c: Coincident(g111,g112)
    c: Coincident(g112,g113)
    c: Vertical(g113)
    c: Coincident(g113,g94)
    c: Coincident(g114,g115)
    c: Coincident(g115,g116)
    c: Coincident(g116,g117)
    c: Coincident(g117,g118)
    c: Coincident(g118,g119)
    c: Coincident(g119,g120)
    c: Coincident(g120,g121)
    c: Coincident(g121,g122)
    c: Coincident(g122,g123)
    c: Coincident(g123,g124)
    c: Coincident(g124,g125)
    c: Coincident(g125,g126)
    c: Coincident(g126,g127)
    c: Coincident(g127,g128)
    c: Coincident(g128,g114)
    c: Coincident(g129,g130)
    c: Horizontal(g130)
    c: Coincident(g130,g131)
    c: Coincident(g131,g132)
    c: Coincident(g132,g133)
    c: Coincident(g133,g129)
FEATURE [Part::FeaturePython] Sketch_On_Surface  # WARN: FeaturePython — macro-defined, semantics opaque (R4)
  ConstructionBounds = true
  FillExtrusion = true
  FillFaces = false
  ReverseU = true
  ReverseV = false
  Sketch = -> Mapped_Sketch
  SwapUV = true
  Thickness = 0
FEATURE [Mesh::Feature] Mesh  label="Aeroplane001 (Meshed)"
FEATURE [Part::Box] Box002  label="Cube002"
  AttacherType = Attacher::AttachEngine3D
  Height = 10
  Length = 10
  Width = 10
FEATURE [Part::Box] Box003  label="Cube003"
  AttacherType = Attacher::AttachEngine3D
  Height = 10
  Length = 10
  Placement = pos=(0,15,0) rot=(0,0,1;0rad)
  Width = 10
